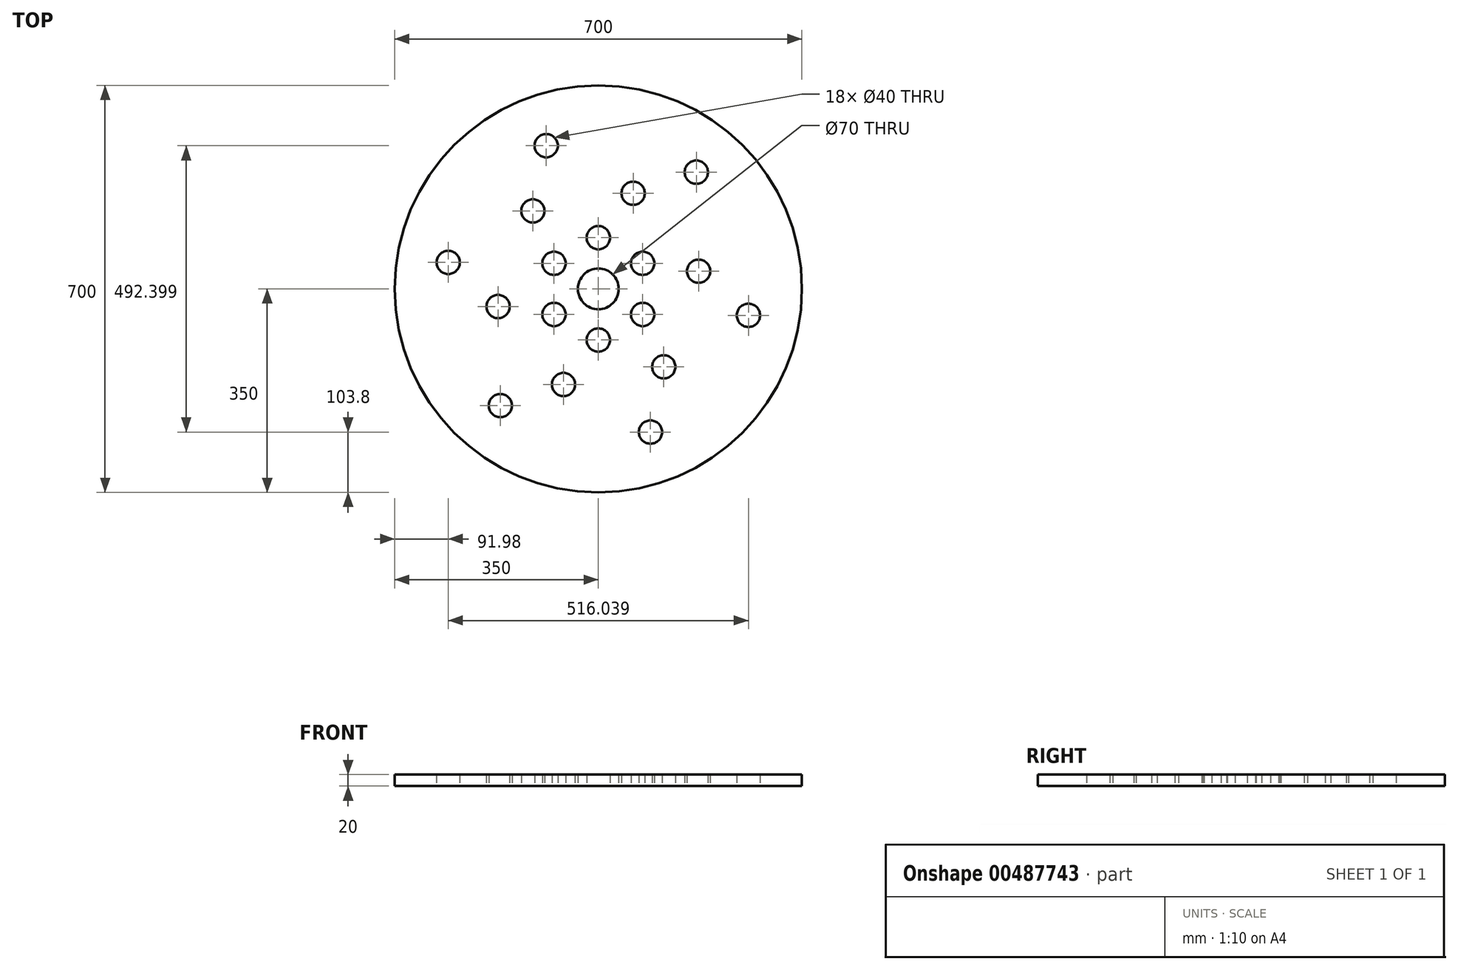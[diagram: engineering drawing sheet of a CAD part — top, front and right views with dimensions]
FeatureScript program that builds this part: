
annotation { "Feature Type Name" : "Feature", "Feature Type Description" : "" }
export const myFeature = defineFeature(function(context is Context, id is Id, definition is map)
    precondition{}
    {
        {
            var Q0;
            Q0=qCreatedBy(makeId("Top.planeOp"),FACE);
            var sketch = newSketch(context, id + "F0", { "sketchPlane" : qUnion([Q0])});
            skCircle(sketch, "E0", {"center": v(0, 0) * mm, "radius": 350 * mm});
            skCircle(sketch, "E1", {"center": v(0, 0) * mm, "radius": 35 * mm});
            skLineSegment(sketch, "E2", {"start": v(0, 0) * mm, "end": v(0, 350) * mm, "construction": true});
            skLineSegment(sketch, "E3", {"start": v(0, 0) * mm, "end": v(119.7, 328.9) * mm, "construction": true});
            skLineSegment(sketch, "E4", {"start": v(0, 0) * mm, "end": v(224.98, 268.12) * mm, "construction": true});
            skCircle(sketch, "E5", {"center": v(0, 88) * mm, "radius": 20 * mm});
            skCircle(sketch, "E6", {"center": v(59.85, 164.45) * mm, "radius": 20 * mm});
            skCircle(sketch, "E7", {"center": v(168.41, 200.7) * mm, "radius": 20 * mm});
            skCircle(sketch, "E8.1.0", {"center": v(-76.21, 44) * mm, "radius": 20 * mm});
            skCircle(sketch, "E8.1.1", {"center": v(-112.49, 134.06) * mm, "radius": 20 * mm});
            skCircle(sketch, "E8.1.2", {"center": v(-89.6, 246.2) * mm, "radius": 20 * mm});
            skCircle(sketch, "E8.2.0", {"center": v(-76.21, -44) * mm, "radius": 20 * mm});
            skCircle(sketch, "E8.2.1", {"center": v(-172.34, -30.39) * mm, "radius": 20 * mm});
            skCircle(sketch, "E8.2.2", {"center": v(-258.02, 45.5) * mm, "radius": 20 * mm});
            skCircle(sketch, "E8.3.0", {"center": v(0, -88) * mm, "radius": 20 * mm});
            skCircle(sketch, "E8.3.1", {"center": v(-59.85, -164.45) * mm, "radius": 20 * mm});
            skCircle(sketch, "E8.3.2", {"center": v(-168.41, -200.7) * mm, "radius": 20 * mm});
            skCircle(sketch, "E8.4.0", {"center": v(76.21, -44) * mm, "radius": 20 * mm});
            skCircle(sketch, "E8.4.1", {"center": v(112.49, -134.06) * mm, "radius": 20 * mm});
            skCircle(sketch, "E8.4.2", {"center": v(89.6, -246.2) * mm, "radius": 20 * mm});
            skCircle(sketch, "E8.5.0", {"center": v(76.21, 44) * mm, "radius": 20 * mm});
            skCircle(sketch, "E8.5.1", {"center": v(172.34, 30.39) * mm, "radius": 20 * mm});
            skCircle(sketch, "E8.5.2", {"center": v(258.02, -45.5) * mm, "radius": 20 * mm});
            skSolve(sketch);
        }
        {
            var Q0;
            Q0=makeQuery(id+"F0.imprint","IMPRINT",FACE,{"disambiguationData":[TD([[makeQuery(id+"F0.imprint","IMPRINT",EDGE,{"derivedFrom":sQuery(id+"F0.wireOp",EDGE,"E0")}),1.0]])]});
            extrude(context, id + "F1", {"entities" : qUnion([Q0]), "depth" : 20 * mm});
        }
    });
